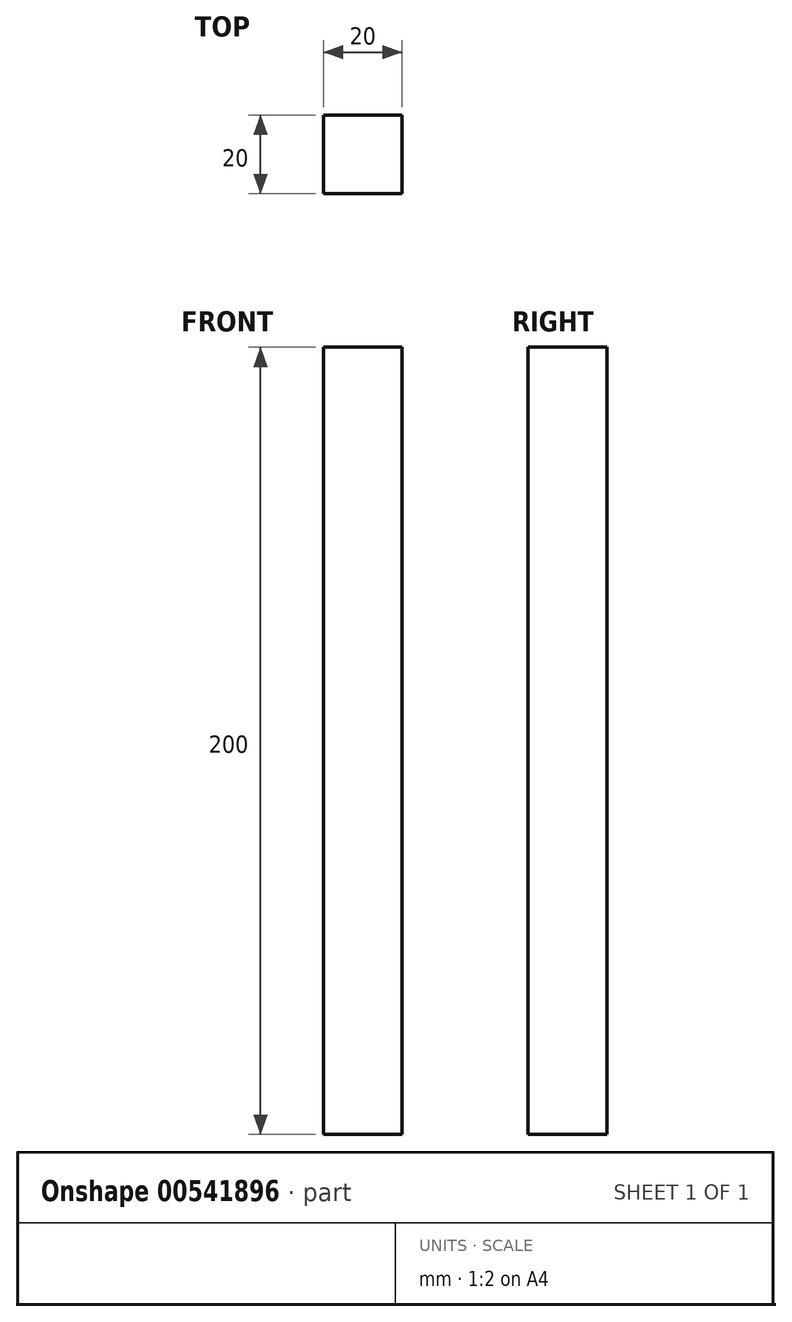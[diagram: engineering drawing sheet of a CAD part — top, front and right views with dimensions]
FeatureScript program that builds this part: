
annotation { "Feature Type Name" : "Feature", "Feature Type Description" : "" }
export const myFeature = defineFeature(function(context is Context, id is Id, definition is map)
    precondition{}
    {
        {
            var Q0;
            Q0=qCreatedBy(makeId("Top.planeOp"),FACE);
            var sketch = newSketch(context, id + "F0", { "sketchPlane" : qUnion([Q0])});
            skLineSegment(sketch, "E0.bottom", {"start": v(-5.8, 14.13) * mm, "end": v(14.2, 14.13) * mm});
            skLineSegment(sketch, "E0.top", {"start": v(-5.8, -5.87) * mm, "end": v(14.2, -5.87) * mm});
            skLineSegment(sketch, "E0.left", {"start": v(-5.8, 14.13) * mm, "end": v(-5.8, -5.87) * mm});
            skLineSegment(sketch, "E0.right", {"start": v(14.2, 14.13) * mm, "end": v(14.2, -5.87) * mm});
            skSolve(sketch);
        }
        {
            var Q0;
            Q0=makeQuery(id+"F0.imprint","IMPRINT",FACE,{"disambiguationData":[TD([[makeQuery(id+"F0.imprint","IMPRINT",EDGE,{"derivedFrom":sQuery(id+"F0.wireOp",EDGE,"E0.bottom")}),-1.0]])]});
            extrude(context, id + "F1", {"entities" : qUnion([Q0]), "depth" : 200 * mm, "offsetDistance" : 25.4 * mm});
        }
    });
